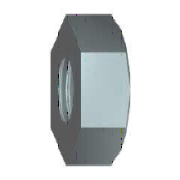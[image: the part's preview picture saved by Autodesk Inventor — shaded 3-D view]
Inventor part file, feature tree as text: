
AUTODESK INVENTOR PART (.ipt)
format: ipt  version: 2015 (Build 190159000, 159)  size: 166,400 bytes
history: native  units: mm
features: other x4, sketch x3, extrude x1, chamfer x1, revolve x1
ambient origin geometry x8: Origin, YZ Plane, XZ Plane, XY Plane, X Axis, Y Axis, Z Axis, Center Point
bodies: Solid1 (feature_tree)
feature tree (10):
  extrude  "Extrusion1"  Depth=10.0mm
  chamfer  "Chamfer1"  Distance=0.5mm
  revolve  "Revolution1"  Angle=45.0deg
  other  "MSC_A1"
  other  "MSC_PT1"
  other  "MSC_PT2"
  other  "MSC_PF1"
  sketch  "Sketch1"  dims[d0=10.0mm d1=5.7mm]
  sketch  "Sketch2"  dims[d2=0.0mm]
  sketch  "Sketch3"  dims[d3=4.917mm d4=6.0mm d5=4.0mm d6=2.0mm d7=90.0deg d8=8.0mm d9=20.594885mm d10=0.5mm d11=2.0mm d12=45.0deg d15=90.0deg d16=0.0mm d17=0.0mm d18=0.0mm d19=0.0mm d21=0.0mm d22=0.0mm d23=0.0mm d32=5.0mm d33=30.0deg]
